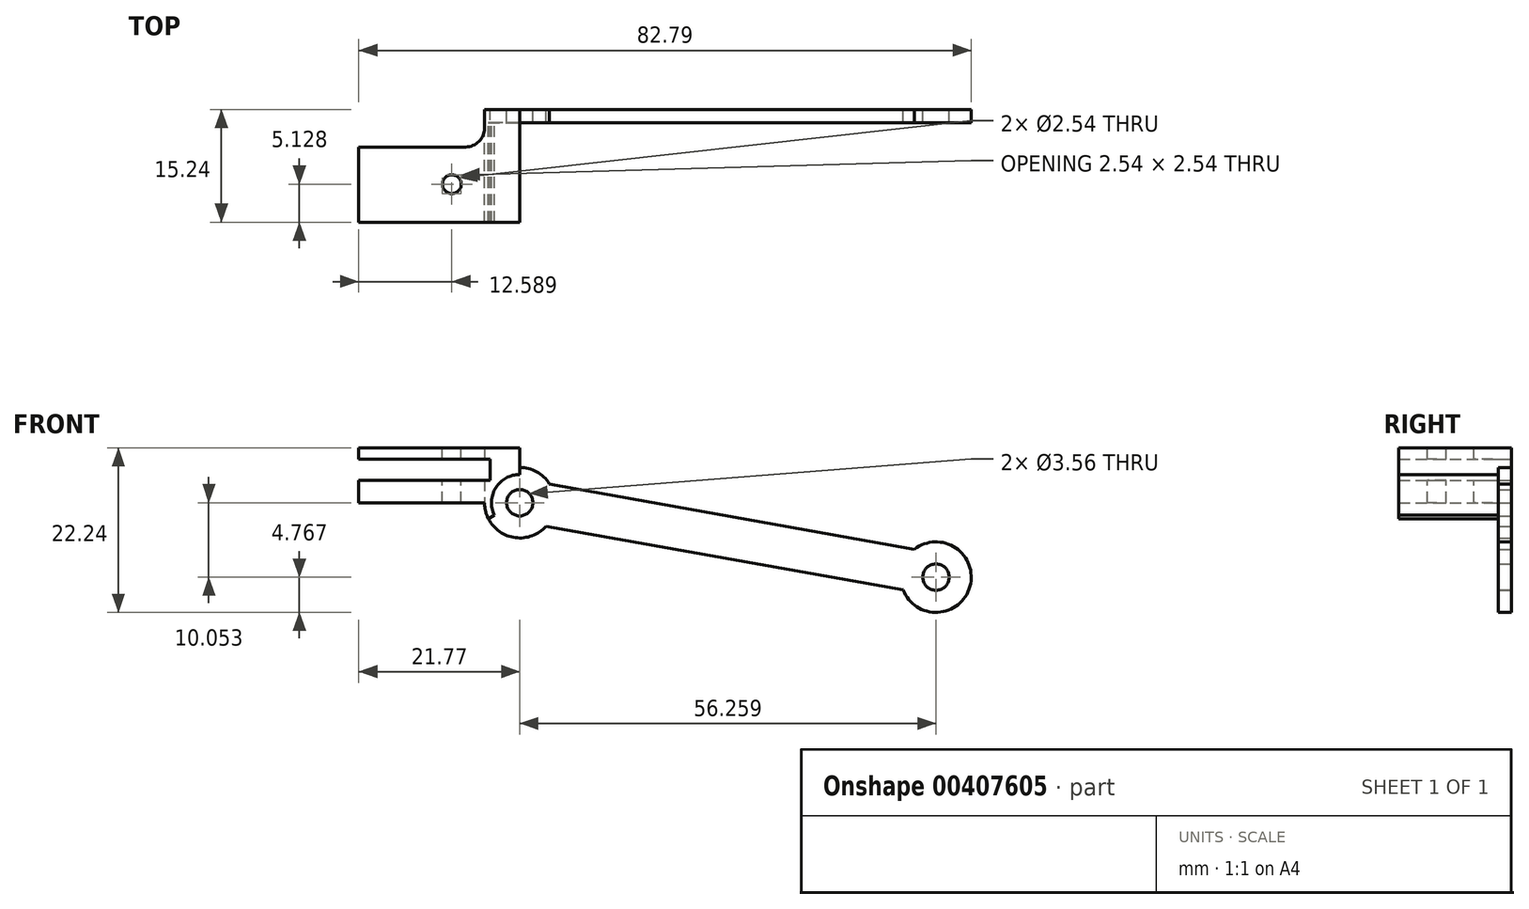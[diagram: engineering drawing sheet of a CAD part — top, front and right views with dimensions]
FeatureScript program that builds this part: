
annotation { "Feature Type Name" : "Feature", "Feature Type Description" : "" }
export const myFeature = defineFeature(function(context is Context, id is Id, definition is map)
    precondition{}
    {
        {
            var Q0;
            Q0=qCreatedBy(makeId("Front.planeOp"),FACE);
            var sketch = newSketch(context, id + "F0", { "sketchPlane" : qUnion([Q0])});
            skLineSegment(sketch, "E0", {"start": v(-5.74, 0) * mm, "end": v(-21.77, 0) * mm});
            skLineSegment(sketch, "E1", {"start": v(-21.77, 0) * mm, "end": v(-21.77, 3.05) * mm});
            skLineSegment(sketch, "E2", {"start": v(-21.77, 3.05) * mm, "end": v(-4, 3.05) * mm});
            skLineSegment(sketch, "E3", {"start": v(-4, 3.05) * mm, "end": v(-4, 5.9) * mm});
            skLineSegment(sketch, "E4", {"start": v(-4, 5.9) * mm, "end": v(-21.77, 5.9) * mm});
            skLineSegment(sketch, "E5", {"start": v(-21.77, 5.9) * mm, "end": v(-21.77, 7.42) * mm});
            skLineSegment(sketch, "E6", {"start": v(-21.77, 7.42) * mm, "end": v(0, 7.42) * mm});
            skLineSegment(sketch, "E7", {"start": v(0, 7.42) * mm, "end": v(0, 4.76) * mm});
            skCircle(sketch, "E8", {"center": v(0, 0) * mm, "radius": 1.78 * mm});
            skCircle(sketch, "E9", {"center": v(56.26, -10.05) * mm, "radius": 1.78 * mm});
            skCircle(sketch, "E10", {"center": v(0, 0) * mm, "radius": 4.76 * mm});
            skCircle(sketch, "E11", {"center": v(56.26, -10.05) * mm, "radius": 4.76 * mm});
            skLineSegment(sketch, "E12", {"start": v(4.03, 2.54) * mm, "end": v(53.36, -6.27) * mm});
            skLineSegment(sketch, "E13", {"start": v(51.83, -11.8) * mm, "end": v(3.56, -3.17) * mm});
            skLineSegment(sketch, "E14", {"start": v(0, 0) * mm, "end": v(56.26, -10.05) * mm, "construction": true});
            skLineSegment(sketch, "E15", {"start": v(-5.74, 0) * mm, "end": v(-4.76, 0) * mm});
            skSolve(sketch);
        }
        {
            var Q0;
            Q0=makeQuery(id+"F0.imprint","IMPRINT",FACE,{"disambiguationData":[TD([[makeQuery(id+"F0.imprint","IMPRINT",EDGE,{"derivedFrom":sQuery(id+"F0.wireOp",EDGE,"E0")}),-1.0]])]});
            var Q1;
            {var subQ0=sQuery(id+"F0.wireOp",EDGE,"E12");Q1=makeQuery(id+"F0.imprint","IMPRINT",FACE,{"disambiguationData":[TD([[makeQuery(id+"F0.imprint","IMPRINT",EDGE,{"derivedFrom":subQ0}),-1.0]])]});}
            var Q2;
            Q2=makeQuery(id+"F0.imprint","IMPRINT",FACE,{"disambiguationData":[TD([[makeQuery(id+"F0.imprint","IMPRINT",EDGE,{"derivedFrom":sQuery(id+"F0.wireOp",EDGE,"E8")}),-1.0]])]});
            var Q3;
            Q3=makeQuery(id+"F0.imprint","IMPRINT",FACE,{"disambiguationData":[TD([[makeQuery(id+"F0.imprint","IMPRINT",EDGE,{"derivedFrom":sQuery(id+"F0.wireOp",EDGE,"E9")}),-1.0]])]});
            extrude(context, id + "F1", {"entities" : qUnion([Q0, Q1, Q2, Q3]), "depth" : 17.78 * mm});
        }
        {
            var Q0;
            Q0=makeQuery(id+"F1.opExtrude","SWEPT_FACE",FACE,{"disambiguationData":[OSD([sQuery(id+"F0.wireOp",EDGE,"E6")])]});
            var sketch = newSketch(context, id + "F2", { "sketchPlane" : qUnion([Q0])});
            skCircle(sketch, "E16", {"center": v(-9.18, -10.11) * mm, "radius": 1.27 * mm});
            skPoint(sketch, "E16.centerSnap0", {"position": v(-21.77, -8.9) * mm});
            skSolve(sketch);
        }
        {
            var Q0;
            Q0=makeQuery(id+"F1.opExtrude","CAP_FACE",FACE,{"disambiguationData":[OSD([sQuery(id+"F0.wireOp",EDGE,"E0"),sQuery(id+"F0.wireOp",EDGE,"E1"),sQuery(id+"F0.wireOp",EDGE,"E2"),sQuery(id+"F0.wireOp",EDGE,"E3"),sQuery(id+"F0.wireOp",EDGE,"E4"),sQuery(id+"F0.wireOp",EDGE,"E5"),sQuery(id+"F0.wireOp",EDGE,"E6"),sQuery(id+"F0.wireOp",EDGE,"E7"),sQuery(id+"F0.wireOp",EDGE,"E8"),sQuery(id+"F0.wireOp",EDGE,"E9"),sQuery(id+"F0.wireOp",EDGE,"E10"),sQuery(id+"F0.wireOp",EDGE,"E11"),sQuery(id+"F0.wireOp",EDGE,"E12"),sQuery(id+"F0.wireOp",EDGE,"E13"),sQuery(id+"F0.wireOp",EDGE,"E15")])],"isStart":false});
            var sketch = newSketch(context, id + "F3", { "sketchPlane" : qUnion([Q0])});
            skLineSegment(sketch, "E17.bottom", {"start": v(0, 7.42) * mm, "end": v(66.1, 7.42) * mm});
            skLineSegment(sketch, "E17.top", {"start": v(-4, -21) * mm, "end": v(66.1, -21) * mm});
            skLineSegment(sketch, "E17.left", {"start": v(-4, -2.6) * mm, "end": v(-4, -21) * mm});
            skLineSegment(sketch, "E17.right", {"start": v(66.1, 7.42) * mm, "end": v(66.1, -21) * mm});
            skArc(sketch, "E18", {"start": v(0, 4.76) * mm, "mid": v(-4.19, 2.27) * mm, "end": v(-4, -2.6) * mm});
            skLineSegment(sketch, "E19", {"start": v(0, 7.42) * mm, "end": v(0, 4.76) * mm});
            skSolve(sketch);
        }
        {
            var Q0;
            {var subQ6=sQuery(id+"F3.wireOp",EDGE,"MmswgulL-DhSU-tjU0-8BoM-CJ2vTl5WkvJw");Q0=makeQuery(id+"F3.imprint","IMPRINT",FACE,{"disambiguationData":[TD([[makeQuery(id+"F3.imprint","IMPRINT",EDGE,{"derivedFrom":subQ6}),-1.0]])]});}
            var Q1;
            Q1=makeQuery(id+"F3.imprint","IMPRINT",FACE,{"disambiguationData":[TD([[makeQuery(id+"F3.imprint","IMPRINT",EDGE,{"derivedFrom":makeQuery(id+"F1.opExtrude","CAP_EDGE",EDGE,{"disambiguationData":[OSD([sQuery(id+"F0.wireOp",EDGE,"E8")])],"isStart":false})}),-1.0]])]});
            extrude(context, id + "F4", {"entities" : qUnion([Q0, Q1]), "operationType" : NewBodyOperationType.REMOVE, "oppositeDirection" : true, "depth" : 16 * mm});
        }
        {
            var Q0;
            Q0=makeQuery(id+"F2.imprint","IMPRINT",FACE,{"disambiguationData":[TD([[makeQuery(id+"F2.imprint","IMPRINT",EDGE,{"derivedFrom":sQuery(id+"F2.wireOp",EDGE,"E16")}),1.0]])]});
            extrude(context, id + "F5", {"entities" : qUnion([Q0]), "operationType" : NewBodyOperationType.REMOVE, "oppositeDirection" : true, "depth" : 25.4 * mm});
        }
        {
            var Q0;
            Q0=makeQuery(id+"F1.opExtrude","CAP_FACE",FACE,{"disambiguationData":[OSD([sQuery(id+"F0.wireOp",EDGE,"E0"),sQuery(id+"F0.wireOp",EDGE,"E1"),sQuery(id+"F0.wireOp",EDGE,"E2"),sQuery(id+"F0.wireOp",EDGE,"E3"),sQuery(id+"F0.wireOp",EDGE,"E4"),sQuery(id+"F0.wireOp",EDGE,"E5"),sQuery(id+"F0.wireOp",EDGE,"E6"),sQuery(id+"F0.wireOp",EDGE,"E7"),sQuery(id+"F0.wireOp",EDGE,"E8"),sQuery(id+"F0.wireOp",EDGE,"E9"),sQuery(id+"F0.wireOp",EDGE,"E10"),sQuery(id+"F0.wireOp",EDGE,"E11"),sQuery(id+"F0.wireOp",EDGE,"E12"),sQuery(id+"F0.wireOp",EDGE,"E13"),sQuery(id+"F0.wireOp",EDGE,"E15")])],"isStart":false});
            var sketch = newSketch(context, id + "F6", { "sketchPlane" : qUnion([Q0])});
            skLineSegment(sketch, "E20.bottom", {"start": v(-26.22, 14.21) * mm, "end": v(3.27, 14.21) * mm});
            skLineSegment(sketch, "E20.top", {"start": v(-26.22, -7.96) * mm, "end": v(3.27, -7.96) * mm});
            skLineSegment(sketch, "E20.left", {"start": v(-26.22, 14.21) * mm, "end": v(-26.22, -7.96) * mm});
            skLineSegment(sketch, "E20.right", {"start": v(3.27, 14.21) * mm, "end": v(3.27, -7.96) * mm});
            skSolve(sketch);
        }
        {
            var Q0;
            Q0=makeQuery(id+"F6.imprint","IMPRINT",FACE,{"disambiguationData":[TD([[makeQuery(id+"F6.imprint","IMPRINT",EDGE,{"derivedFrom":makeQuery(id+"F1.opExtrude","CAP_EDGE",EDGE,{"disambiguationData":[OSD([sQuery(id+"F0.wireOp",EDGE,"E0")])],"isStart":false})}),-1.0]])]});
            extrude(context, id + "F7", {"entities" : qUnion([Q0]), "operationType" : NewBodyOperationType.REMOVE, "oppositeDirection" : true, "depth" : 2.54 * mm});
        }
        {
            var Q0;
            Q0=makeQuery(id+"F1.opExtrude","CAP_FACE",FACE,{"disambiguationData":[OSD([sQuery(id+"F0.wireOp",EDGE,"E0"),sQuery(id+"F0.wireOp",EDGE,"E1"),sQuery(id+"F0.wireOp",EDGE,"E2"),sQuery(id+"F0.wireOp",EDGE,"E3"),sQuery(id+"F0.wireOp",EDGE,"E4"),sQuery(id+"F0.wireOp",EDGE,"E5"),sQuery(id+"F0.wireOp",EDGE,"E6"),sQuery(id+"F0.wireOp",EDGE,"E7"),sQuery(id+"F0.wireOp",EDGE,"E8"),sQuery(id+"F0.wireOp",EDGE,"E9"),sQuery(id+"F0.wireOp",EDGE,"E10"),sQuery(id+"F0.wireOp",EDGE,"E11"),sQuery(id+"F0.wireOp",EDGE,"E12"),sQuery(id+"F0.wireOp",EDGE,"E13"),sQuery(id+"F0.wireOp",EDGE,"E15")])],"isStart":true});
            var sketch = newSketch(context, id + "F8", { "sketchPlane" : qUnion([Q0])});
            skLineSegment(sketch, "E21.bottom", {"start": v(21.77, 14.93) * mm, "end": v(4.78, 14.93) * mm});
            skLineSegment(sketch, "E21.top", {"start": v(21.77, -16.88) * mm, "end": v(4.78, -16.88) * mm});
            skLineSegment(sketch, "E21.left", {"start": v(4.78, 14.93) * mm, "end": v(4.78, -16.88) * mm});
            skLineSegment(sketch, "E21.right", {"start": v(21.77, 14.93) * mm, "end": v(21.77, -16.88) * mm});
            skSolve(sketch);
        }
        {
            var Q0;
            {var subQ0=sQuery(id+"F8.wireOp",EDGE,"E21.left");var subQ1=makeQuery(id+"F1.opExtrude","CAP_EDGE",EDGE,{"disambiguationData":[OSD([sQuery(id+"F0.wireOp",EDGE,"E6")])],"isStart":true});var subQ2=makeQuery(id+"F8.imprint","INTERSECT",VERTEX,{"derivedFrom":[subQ1,subQ0]});Q0=makeQuery(id+"F8.imprint","IMPRINT",FACE,{"disambiguationData":[TD([[makeQuery(id+"F8.imprint","IMPRINT",EDGE,{"disambiguationData":[TD([[subQ2,-1.0]])],"derivedFrom":subQ0}),1.0]])]});}
            var Q1;
            {var subQ3=makeQuery(id+"F1.opExtrude","CAP_EDGE",EDGE,{"disambiguationData":[OSD([sQuery(id+"F0.wireOp",EDGE,"E2")])],"isStart":true});var subQ5=sQuery(id+"F8.wireOp",EDGE,"E21.right");var subQ7=makeQuery(id+"F8.imprint","INTERSECT",VERTEX,{"derivedFrom":[subQ3,subQ5]});Q1=makeQuery(id+"F8.imprint","IMPRINT",FACE,{"disambiguationData":[TD([[makeQuery(id+"F8.imprint","IMPRINT",EDGE,{"disambiguationData":[TD([[subQ7,-1.0]])],"derivedFrom":subQ3}),1.0]])]});}
            extrude(context, id + "F9", {"entities" : qUnion([Q0, Q1]), "operationType" : NewBodyOperationType.REMOVE, "oppositeDirection" : true, "depth" : 5.08 * mm});
        }
        {
            var Q0;
            Q0=makeQuery(id+"F4.boolean.opBoolean","COPY",FACE,{"derivedFrom":makeQuery(id+"F4.opExtrude","CAP_FACE",FACE,{"disambiguationData":[OSD([sQuery(id+"F0.wireOp",EDGE,"E8"),sQuery(id+"F0.wireOp",EDGE,"E9"),sQuery(id+"F0.wireOp",EDGE,"E10"),sQuery(id+"F0.wireOp",EDGE,"E11"),sQuery(id+"F0.wireOp",EDGE,"E12"),sQuery(id+"F0.wireOp",EDGE,"E13"),sQuery(id+"F3.wireOp",EDGE,"E18")])],"isStart":false})});
            var sketch = newSketch(context, id + "F10", { "sketchPlane" : qUnion([Q0])});
            skCircle(sketch, "E22", {"center": v(0, 0) * mm, "radius": 3.82 * mm});
            skCircle(sketch, "E23", {"center": v(0, 0) * mm, "radius": 5.07 * mm});
            skLineSegment(sketch, "E24", {"start": v(0, 3.82) * mm, "end": v(0, 5.07) * mm});
            skLineSegment(sketch, "E25", {"start": v(-3.82, 0) * mm, "end": v(-5.07, 0) * mm});
            skLineSegment(sketch, "E26", {"start": v(-3.43, -1.66) * mm, "end": v(-4.5, -2.35) * mm});
            skSolve(sketch);
        }
        {
            var Q0;
            {var subQ0=sQuery(id+"F10.wireOp",EDGE,"E24");var subQ1=sQuery(id+"F10.wireOp",EDGE,"E22");var subQ2=makeQuery(id+"F10.imprint","INTERSECT",VERTEX,{"derivedFrom":[subQ1,subQ0]});Q0=makeQuery(id+"F10.imprint","IMPRINT",FACE,{"disambiguationData":[TD([[makeQuery(id+"F10.imprint","IMPRINT",EDGE,{"disambiguationData":[TD([[subQ2,-1.0]])],"derivedFrom":subQ1}),-1.0]])]});}
            var Q1;
            {var subQ0=sQuery(id+"F10.wireOp",EDGE,"E25");var subQ1=sQuery(id+"F10.wireOp",EDGE,"E22");var subQ2=makeQuery(id+"F10.imprint","INTERSECT",VERTEX,{"derivedFrom":[subQ1,subQ0]});Q1=makeQuery(id+"F10.imprint","IMPRINT",FACE,{"disambiguationData":[TD([[makeQuery(id+"F10.imprint","IMPRINT",EDGE,{"disambiguationData":[TD([[subQ2,-1.0]])],"derivedFrom":subQ1}),-1.0]])]});}
            var Q2;
            Q2=makeQuery(id+"F7.boolean.opBoolean","COPY",FACE,{"derivedFrom":makeQuery(id+"F7.opExtrude","CAP_FACE",FACE,{"disambiguationData":[OSD([sQuery(id+"F0.wireOp",EDGE,"E0"),sQuery(id+"F0.wireOp",EDGE,"E1"),sQuery(id+"F0.wireOp",EDGE,"E2"),sQuery(id+"F0.wireOp",EDGE,"E3"),sQuery(id+"F0.wireOp",EDGE,"E4"),sQuery(id+"F0.wireOp",EDGE,"E5"),sQuery(id+"F0.wireOp",EDGE,"E6"),sQuery(id+"F0.wireOp",EDGE,"E7"),sQuery(id+"F0.wireOp",EDGE,"E10"),sQuery(id+"F0.wireOp",EDGE,"E15"),sQuery(id+"F3.wireOp",EDGE,"E18")])],"isStart":false})});
            extrude(context, id + "F11", {"entities" : qUnion([Q0, Q1]), "operationType" : NewBodyOperationType.ADD, "endBound" : BoundingType.UP_TO_SURFACE, "endBoundEntityFace" : qUnion([Q2]), "depth" : 25.4 * mm});
        }
        {
            var Q0;
            {var subQ0=sQuery(id+"F8.wireOp",EDGE,"E21.left");Q0=makeQuery(id+"F9.boolean.opBoolean","COPY",EDGE,{"derivedFrom":makeQuery(id+"F9.opExtrude","CAP_EDGE",EDGE,{"disambiguationData":[OSD([subQ0]),TDD([makeQuery(id+"F8.imprint","IMPRINT",EDGE,{"disambiguationData":[TD([[makeQuery(id+"F8.imprint","INTERSECT",VERTEX,{"derivedFrom":[makeQuery(id+"F1.opExtrude","CAP_EDGE",EDGE,{"disambiguationData":[OSD([sQuery(id+"F0.wireOp",EDGE,"E2")])],"isStart":true}),subQ0]}),-1.0]])],"derivedFrom":subQ0})])],"isStart":false})});}
            var Q1;
            {var subQ0=sQuery(id+"F8.wireOp",EDGE,"E21.left");Q1=makeQuery(id+"F9.boolean.opBoolean","COPY",EDGE,{"derivedFrom":makeQuery(id+"F9.opExtrude","CAP_EDGE",EDGE,{"disambiguationData":[OSD([subQ0]),TDD([makeQuery(id+"F8.imprint","IMPRINT",EDGE,{"disambiguationData":[TD([[makeQuery(id+"F8.imprint","INTERSECT",VERTEX,{"derivedFrom":[makeQuery(id+"F1.opExtrude","CAP_EDGE",EDGE,{"disambiguationData":[OSD([sQuery(id+"F0.wireOp",EDGE,"E6")])],"isStart":true}),subQ0]}),-1.0]])],"derivedFrom":subQ0})])],"isStart":false})});}
            fillet(context, id + "F12", {"entities" : qUnion([Q0, Q1]), "radius" : 2.54 * mm, "tangentPropagation" : true, "allowEdgeOverflow" : false});
        }
    });
